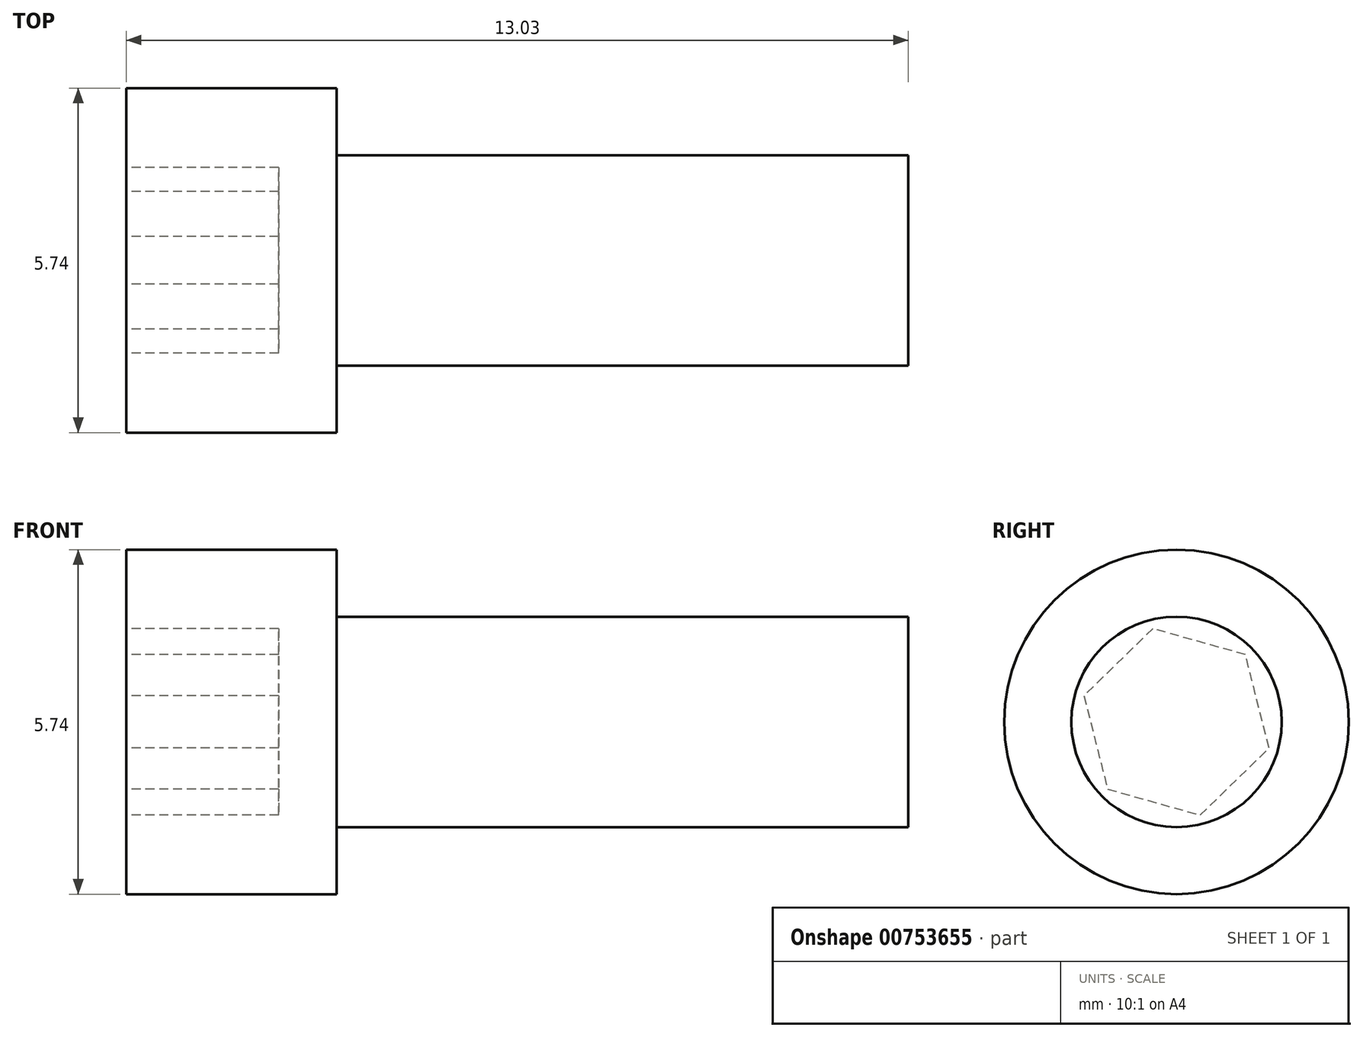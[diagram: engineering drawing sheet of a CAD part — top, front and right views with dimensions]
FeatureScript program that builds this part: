
annotation { "Feature Type Name" : "Feature", "Feature Type Description" : "" }
export const myFeature = defineFeature(function(context is Context, id is Id, definition is map)
    precondition{}
    {
        {
            var Q0;
            Q0=qCreatedBy(makeId("Top.planeOp"),FACE);
            var sketch = newSketch(context, id + "F0", { "sketchPlane" : qUnion([Q0])});
            skLineSegment(sketch, "E0", {"start": v(0, 0) * mm, "end": v(0, 2.87) * mm});
            skLineSegment(sketch, "E1", {"start": v(0, 2.87) * mm, "end": v(3.5, 2.87) * mm});
            skLineSegment(sketch, "E2", {"start": v(3.5, 2.87) * mm, "end": v(3.5, 1.75) * mm});
            skLineSegment(sketch, "E3", {"start": v(3.5, 1.75) * mm, "end": v(13.03, 1.75) * mm});
            skLineSegment(sketch, "E4", {"start": v(13.03, 1.75) * mm, "end": v(13.03, 0) * mm});
            skLineSegment(sketch, "E5", {"start": v(0, 0) * mm, "end": v(13.03, 0) * mm});
            skLineSegment(sketch, "E6", {"start": v(11.26, 0) * mm, "end": v(-1.57, 0) * mm, "construction": true});
            skSolve(sketch);
        }
        {
            var Q0;
            Q0=makeQuery(id+"F0.imprint","IMPRINT",FACE,{"disambiguationData":[TD([[makeQuery(id+"F0.imprint","IMPRINT",EDGE,{"derivedFrom":sQuery(id+"F0.wireOp",EDGE,"E0")}),-1.0]])]});
            var Q1;
            Q1=sQuery(id+"F0.wireOp",EDGE,"E6");
            revolve(context, id + "F1", {"surfaceOperationType" : NewSurfaceOperationType.NEW, "entities" : qUnion([Q0]), "axis" : qUnion([Q1]), "revolveType" : RevolveType.FULL});
        }
        {
            var Q0;
            Q0=makeQuery(id+"F1.opRevolve","SWEPT_FACE",FACE,{"disambiguationData":[OSD([sQuery(id+"F0.wireOp",EDGE,"E0")])]});
            var sketch = newSketch(context, id + "F2", { "sketchPlane" : qUnion([Q0])});
            skCircle(sketch, "E7.cCircle", {"center": v(0, 0) * mm, "radius": 1.39 * mm, "construction": true});
            skLineSegment(sketch, "E7.0", {"start": v(0.4, 1.55) * mm, "end": v(1.54, 0.43) * mm});
            skLineSegment(sketch, "E7.1", {"start": v(1.54, 0.43) * mm, "end": v(1.15, -1.12) * mm});
            skLineSegment(sketch, "E7.2", {"start": v(1.15, -1.12) * mm, "end": v(-0.4, -1.55) * mm});
            skLineSegment(sketch, "E7.3", {"start": v(-0.4, -1.55) * mm, "end": v(-1.54, -0.43) * mm});
            skLineSegment(sketch, "E7.4", {"start": v(-1.54, -0.43) * mm, "end": v(-1.15, 1.12) * mm});
            skLineSegment(sketch, "E7.5", {"start": v(-1.15, 1.12) * mm, "end": v(0.4, 1.55) * mm});
            skPoint(sketch, "E7.0.midPoint", {"position": v(0.97, 1) * mm});
            skSolve(sketch);
        }
        {
            var Q0;
            Q0=makeQuery(id+"F2.imprint","IMPRINT",FACE,{"disambiguationData":[TD([[makeQuery(id+"F2.imprint","IMPRINT",EDGE,{"derivedFrom":sQuery(id+"F2.wireOp",EDGE,"E7.0")}),-1.0]])]});
            extrude(context, id + "F3", {"entities" : qUnion([Q0]), "operationType" : NewBodyOperationType.REMOVE, "oppositeDirection" : true, "depth" : 2.54 * mm, "offsetDistance" : 25.4 * mm});
        }
    });
